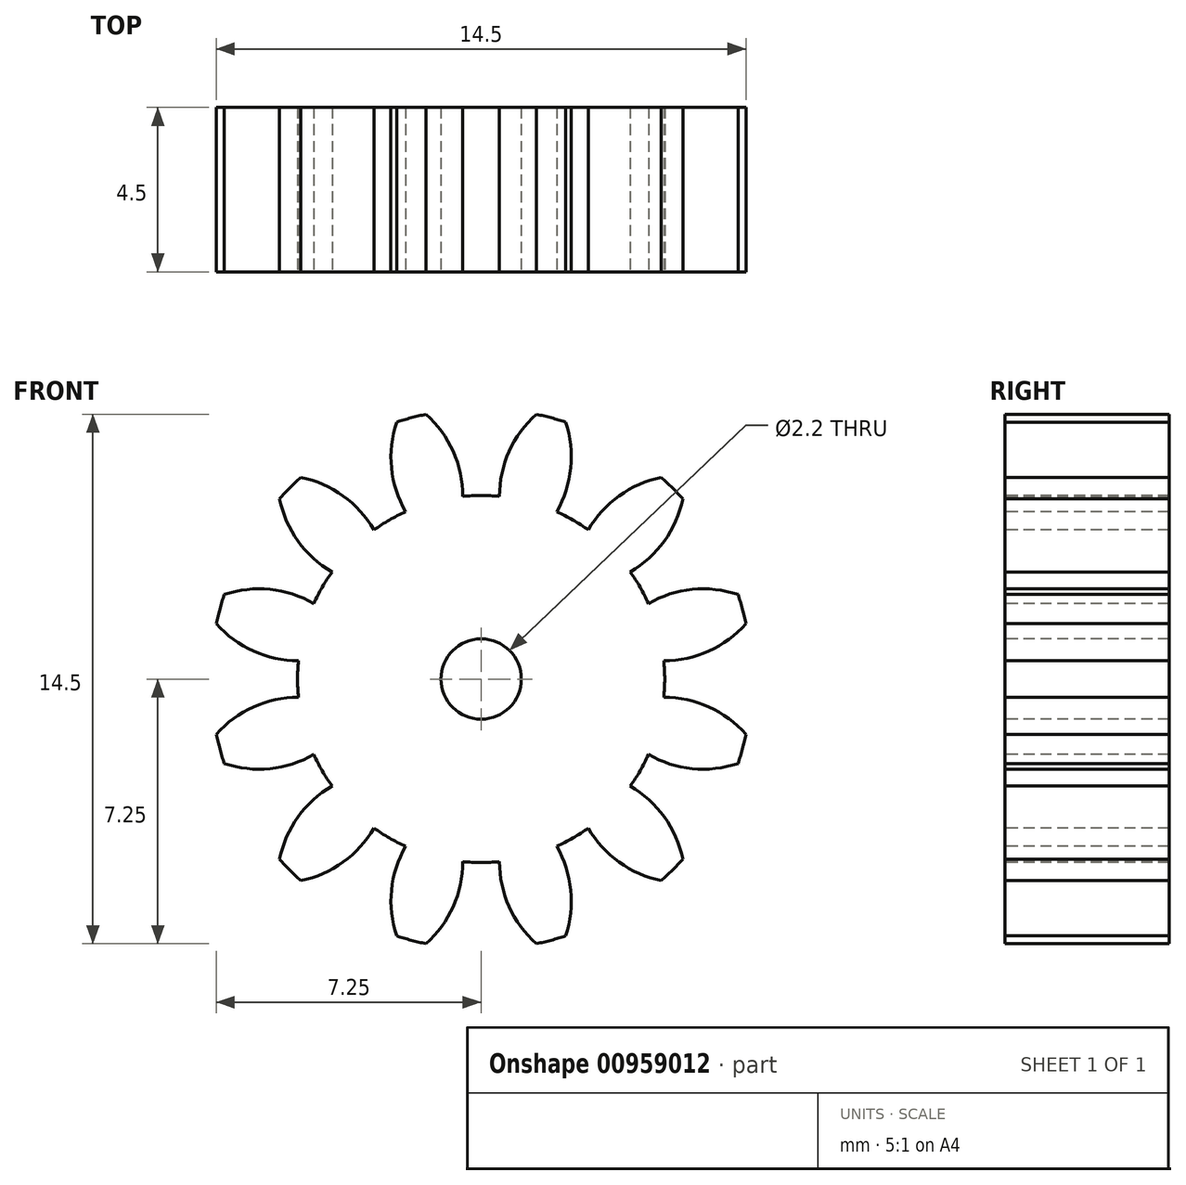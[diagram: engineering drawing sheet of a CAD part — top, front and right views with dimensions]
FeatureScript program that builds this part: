
annotation { "Feature Type Name" : "Feature", "Feature Type Description" : "" }
export const myFeature = defineFeature(function(context is Context, id is Id, definition is map)
    precondition{}
    {
        {
            var Q0;
            Q0=qCreatedBy(makeId("Front.planeOp"),FACE);
            var sketch = newSketch(context, id + "F0", { "sketchPlane" : qUnion([Q0])});
            skCircle(sketch, "E0", {"center": v(0, 0) * mm, "radius": 7.4 * mm});
            skSolve(sketch);
        }
        {
            var Q0;
            Q0 = qSketchRegion(id + "F0", true);
            extrude(context, id + "F1", {"entities" : qUnion([Q0]), "depth" : 4.5 * mm, "offsetDistance" : 25.4 * mm});
        }
        {
            var Q0;
            Q0=makeQuery(id+"F1.opExtrude","CAP_FACE",FACE,{"disambiguationData":[OSD([sQuery(id+"F0.wireOp",EDGE,"E0")])],"isStart":false});
            var sketch = newSketch(context, id + "F2", { "sketchPlane" : qUnion([Q0])});
            skArc(sketch, "E1", {"start": v(0.5, 5) * mm, "mid": v(0, 5.03) * mm, "end": v(-0.5, 5) * mm});
            skLineSegment(sketch, "E2", {"start": v(0, 7.4) * mm, "end": v(0, -7.4) * mm, "construction": true});
            skLineSegment(sketch, "E3", {"start": v(-1.51, 7.25) * mm, "end": v(1.51, 7.25) * mm, "construction": true});
            skLineSegment(sketch, "E4", {"start": v(-5.46, 5) * mm, "end": v(5.46, 5) * mm, "construction": true});
            skArc(sketch, "E5", {"start": v(-0.5, 5) * mm, "mid": v(-0.76, 6.23) * mm, "end": v(-1.51, 7.25) * mm});
            skArc(sketch, "E6.MirrorCS", {"start": v(0.5, 5) * mm, "mid": v(0.76, 6.23) * mm, "end": v(1.51, 7.25) * mm});
            skArc(sketch, "E7", {"start": v(1.51, 7.25) * mm, "mid": v(0, 7.4) * mm, "end": v(-1.51, 7.25) * mm});
            skSolve(sketch);
        }
        {
            var Q0;
            {var subQ5=sQuery(id+"F2.wireOp",EDGE,"E7");Q0=makeQuery(id+"F2.imprint","IMPRINT",FACE,{"disambiguationData":[TD([[makeQuery(id+"F2.imprint","IMPRINT",EDGE,{"derivedFrom":subQ5}),1.0]])]});}
            extrude(context, id + "F3", {"entities" : qUnion([Q0]), "operationType" : NewBodyOperationType.REMOVE, "endBound" : BoundingType.THROUGH_ALL, "oppositeDirection" : true, "depth" : 25.4 * mm, "offsetDistance" : 25.4 * mm});
        }
        {
            var Q0;
            Q0=makeQuery(id+"F3.boolean.opBoolean","COPY",FACE,{"derivedFrom":makeQuery(id+"F3.opExtrude","SWEPT_FACE",FACE,{"disambiguationData":[OSD([sQuery(id+"F2.wireOp",EDGE,"E6.MirrorCS")])]})});
            var Q1;
            Q1=makeQuery(id+"F3.boolean.opBoolean","COPY",FACE,{"derivedFrom":makeQuery(id+"F3.opExtrude","SWEPT_FACE",FACE,{"disambiguationData":[OSD([sQuery(id+"F2.wireOp",EDGE,"E1")])]})});
            var Q2;
            Q2=makeQuery(id+"F3.boolean.opBoolean","COPY",FACE,{"derivedFrom":makeQuery(id+"F3.opExtrude","SWEPT_FACE",FACE,{"disambiguationData":[OSD([sQuery(id+"F2.wireOp",EDGE,"E5")])]})});
            var Q3;
            Q3=makeQuery(id+"F1.opExtrude","SWEPT_FACE",FACE,{"disambiguationData":[OSD([sQuery(id+"F0.wireOp",EDGE,"E0")])]});
            circularPattern(context, id + "F4", {"patternType" : PatternType.FACE, "faces" : qUnion([Q0, Q1, Q2]), "axis" : qUnion([Q3]), "angle" : 360 * degree, "instanceCount" : 12, "equalSpace" : true});
        }
        {
            var Q0;
            Q0=makeQuery(id+"F1.opExtrude","CAP_FACE",FACE,{"disambiguationData":[OSD([sQuery(id+"F0.wireOp",EDGE,"E0")])],"isStart":false});
            var sketch = newSketch(context, id + "F5", { "sketchPlane" : qUnion([Q0])});
            skCircle(sketch, "E8", {"center": v(0, 0) * mm, "radius": 1.1 * mm});
            skSolve(sketch);
        }
        {
            var Q0;
            Q0=makeQuery(id+"F5.imprint","IMPRINT",FACE,{"disambiguationData":[TD([[makeQuery(id+"F5.imprint","IMPRINT",EDGE,{"derivedFrom":sQuery(id+"F5.wireOp",EDGE,"E8")}),1.0]])]});
            extrude(context, id + "F6", {"entities" : qUnion([Q0]), "operationType" : NewBodyOperationType.REMOVE, "endBound" : BoundingType.THROUGH_ALL, "oppositeDirection" : true, "depth" : 25.4 * mm, "offsetDistance" : 25.4 * mm});
        }
    });
